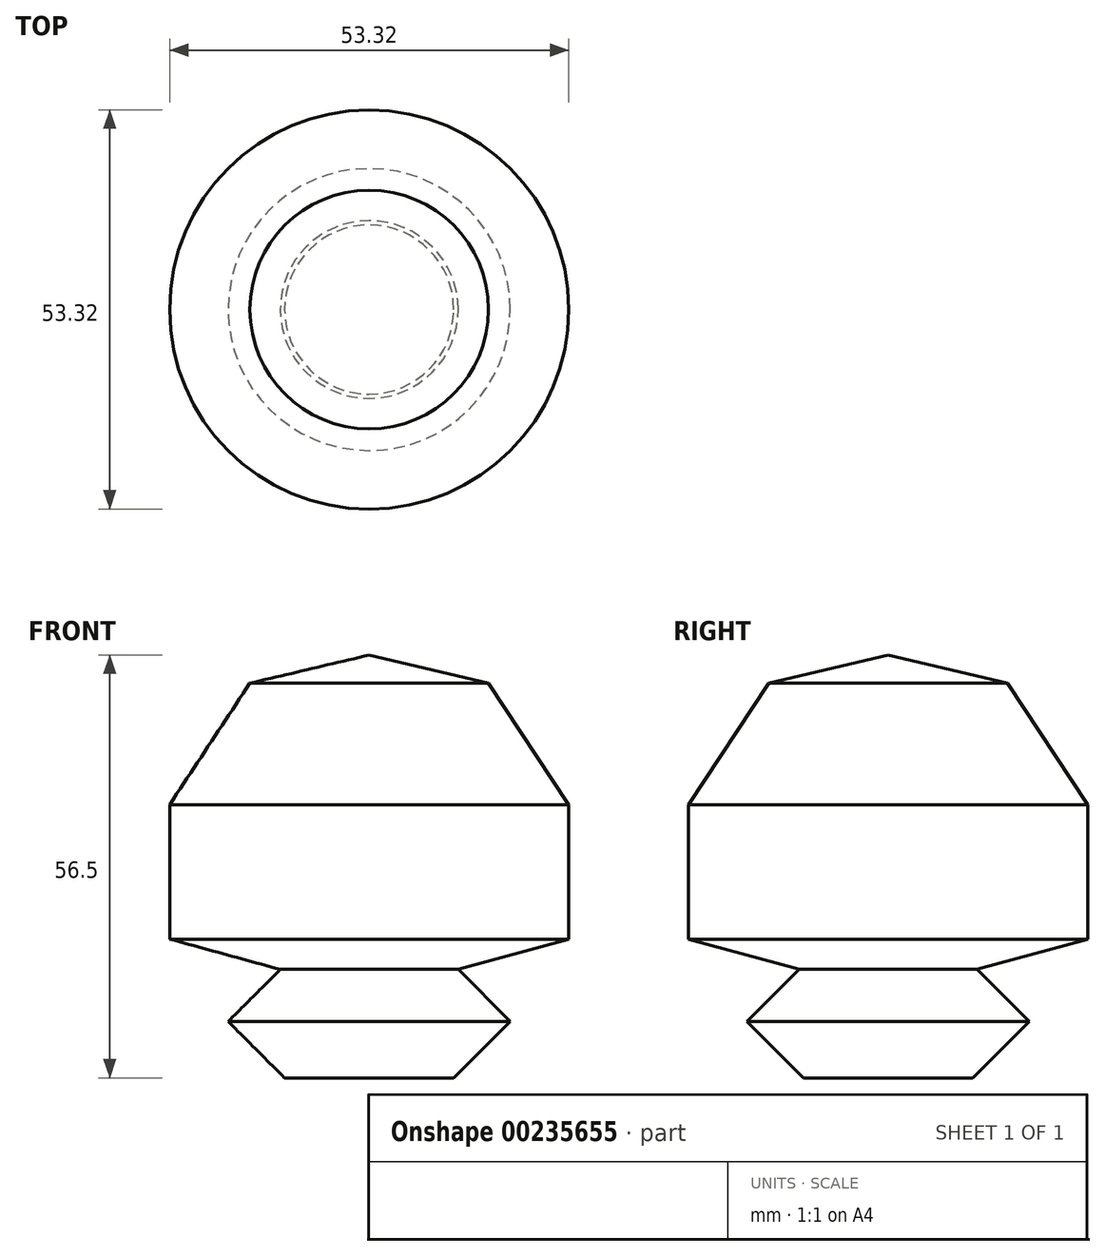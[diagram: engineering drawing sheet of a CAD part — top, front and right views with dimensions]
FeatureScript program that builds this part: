
annotation { "Feature Type Name" : "Feature", "Feature Type Description" : "" }
export const myFeature = defineFeature(function(context is Context, id is Id, definition is map)
    precondition{}
    {
        {
            var Q0;
            Q0=qCreatedBy(makeId("Front.planeOp"),FACE);
            var sketch = newSketch(context, id + "F0", { "sketchPlane" : qUnion([Q0])});
            skLineSegment(sketch, "E0", {"start": v(0, 56.5) * mm, "end": v(-15.94, 52.74) * mm});
            skLineSegment(sketch, "E1", {"start": v(-15.94, 52.74) * mm, "end": v(-26.66, 36.5) * mm});
            skLineSegment(sketch, "E2", {"start": v(-26.66, 36.5) * mm, "end": v(-26.66, 18.54) * mm});
            skLineSegment(sketch, "E3", {"start": v(-26.66, 18.54) * mm, "end": v(-11.88, 14.49) * mm});
            skLineSegment(sketch, "E4", {"start": v(-11.88, 14.49) * mm, "end": v(-18.83, 7.53) * mm});
            skLineSegment(sketch, "E5", {"start": v(-18.83, 7.53) * mm, "end": v(-11.3, 0) * mm});
            skLineSegment(sketch, "E6", {"start": v(-11.3, 0) * mm, "end": v(0, 0) * mm});
            skLineSegment(sketch, "E7", {"start": v(0, 0) * mm, "end": v(0, 56.5) * mm});
            skSolve(sketch);
        }
        {
            var Q0;
            Q0=makeQuery(id+"F0.imprint","IMPRINT",FACE,{"disambiguationData":[TD([[makeQuery(id+"F0.imprint","IMPRINT",EDGE,{"derivedFrom":sQuery(id+"F0.wireOp",EDGE,"E0")}),1.0]])]});
            var Q1;
            Q1=sQuery(id+"F0.wireOp",EDGE,"E7");
            revolve(context, id + "F1", {"entities" : qUnion([Q0]), "axis" : qUnion([Q1]), "revolveType" : RevolveType.FULL});
        }
    });
